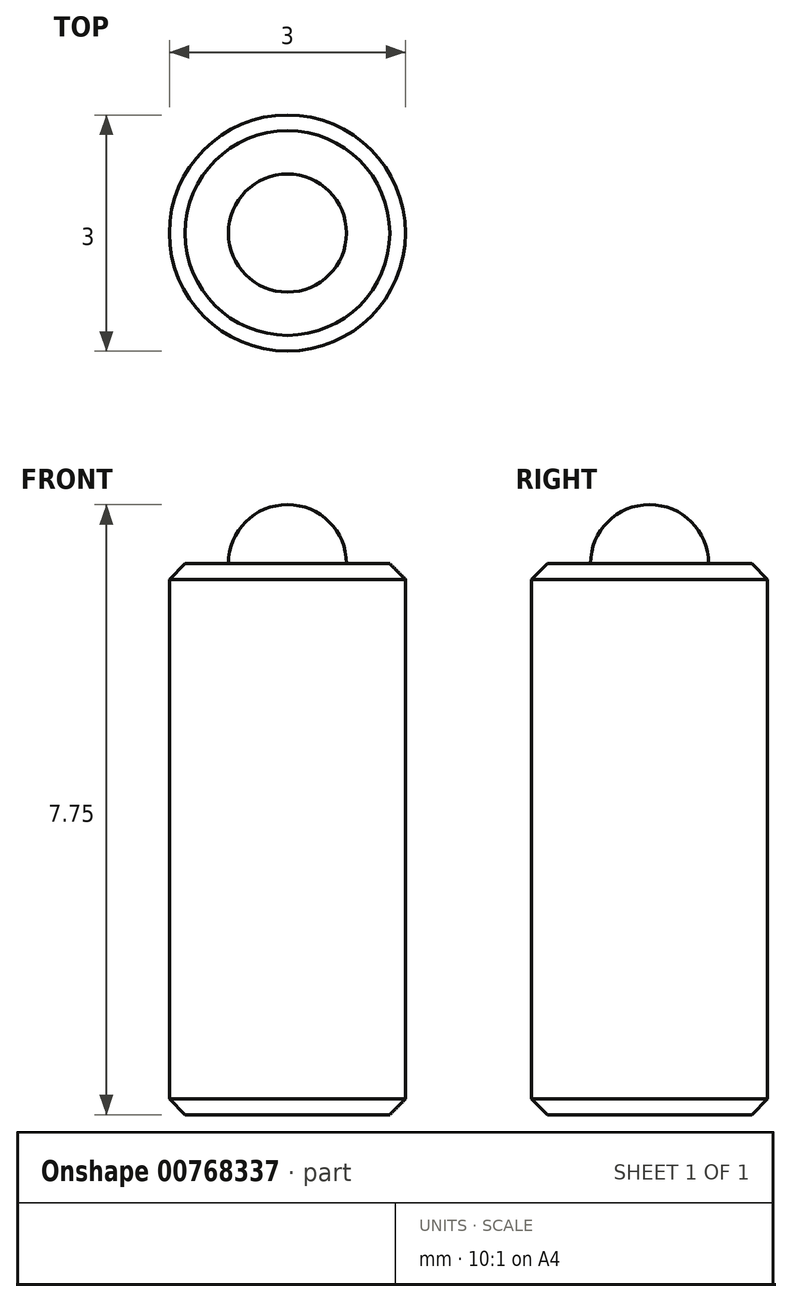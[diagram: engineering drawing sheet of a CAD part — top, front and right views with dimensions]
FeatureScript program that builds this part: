
annotation { "Feature Type Name" : "Feature", "Feature Type Description" : "" }
export const myFeature = defineFeature(function(context is Context, id is Id, definition is map)
    precondition{}
    {
        {
            var Q0;
            Q0=qCreatedBy(makeId("Top.planeOp"),FACE);
            var sketch = newSketch(context, id + "F0", { "sketchPlane" : qUnion([Q0])});
            skCircle(sketch, "E0", {"center": v(0, 0) * mm, "radius": 1.5 * mm});
            skSolve(sketch);
        }
        {
            var Q0;
            Q0 = qSketchRegion(id + "F0", true);
            extrude(context, id + "F1", {"entities" : qUnion([Q0]), "depth" : 7 * mm, "offsetDistance" : 25 * mm});
        }
        {
            var Q0;
            Q0=makeQuery(id+"F1.opExtrude","CAP_FACE",FACE,{"disambiguationData":[OSD([sQuery(id+"F0.wireOp",EDGE,"E0")])],"isStart":false});
            var sketch = newSketch(context, id + "F2", { "sketchPlane" : qUnion([Q0])});
            skLineSegment(sketch, "E1", {"start": v(0, -1.5) * mm, "end": v(0, 1.5) * mm});
            skSolve(sketch);
        }
        {
            var Q0;
            {var subQ0=sQuery(id+"F2.wireOp",EDGE,"E1");Q0=makeQuery(id+"F2.imprint","IMPRINT",FACE,{"disambiguationData":[TD([[makeQuery(id+"F2.imprint","IMPRINT",EDGE,{"derivedFrom":subQ0}),1.0]])]});}
            var sketch = newSketch(context, id + "F3", { "sketchPlane" : qUnion([Q0])});
            skCircle(sketch, "E2", {"center": v(0, 0) * mm, "radius": 0.75 * mm});
            skSolve(sketch);
        }
        {
            var Q0;
            {var subQ0=sQuery(id+"F3.wireOp",EDGE,"E2");var subQ1=makeQuery(id+"F2.imprint","IMPRINT",EDGE,{"derivedFrom":sQuery(id+"F2.wireOp",EDGE,"E1")});var subQ2=makeQuery(id+"F3.imprint","INTERSECT",VERTEX,{"disambiguationData":[OD(0.0)],"derivedFrom":[subQ1,subQ0]});Q0=makeQuery(id+"F3.imprint","IMPRINT",FACE,{"disambiguationData":[TD([[makeQuery(id+"F3.imprint","IMPRINT",EDGE,{"disambiguationData":[TD([[subQ2,-1.0]])],"derivedFrom":subQ0}),1.0]])]});}
            var Q1;
            Q1=sQuery(id+"F2.wireOp",EDGE,"E1");
            revolve(context, id + "F4", {"operationType" : NewBodyOperationType.ADD, "surfaceOperationType" : NewSurfaceOperationType.NEW, "entities" : qUnion([Q0]), "axis" : qUnion([Q1]), "revolveType" : RevolveType.FULL});
        }
        {
            var Q0;
            Q0=makeQuery(id+"F1.opExtrude","CAP_EDGE",EDGE,{"disambiguationData":[OSD([sQuery(id+"F0.wireOp",EDGE,"E0")])],"isStart":false});
            var Q1;
            Q1=makeQuery(id+"F1.opExtrude","CAP_EDGE",EDGE,{"disambiguationData":[OSD([sQuery(id+"F0.wireOp",EDGE,"E0")])],"isStart":true});
            chamfer(context, id + "F5", {"entities" : qUnion([Q0, Q1]), "width" : 0.2 * mm, "tangentPropagation" : true});
        }
    });
